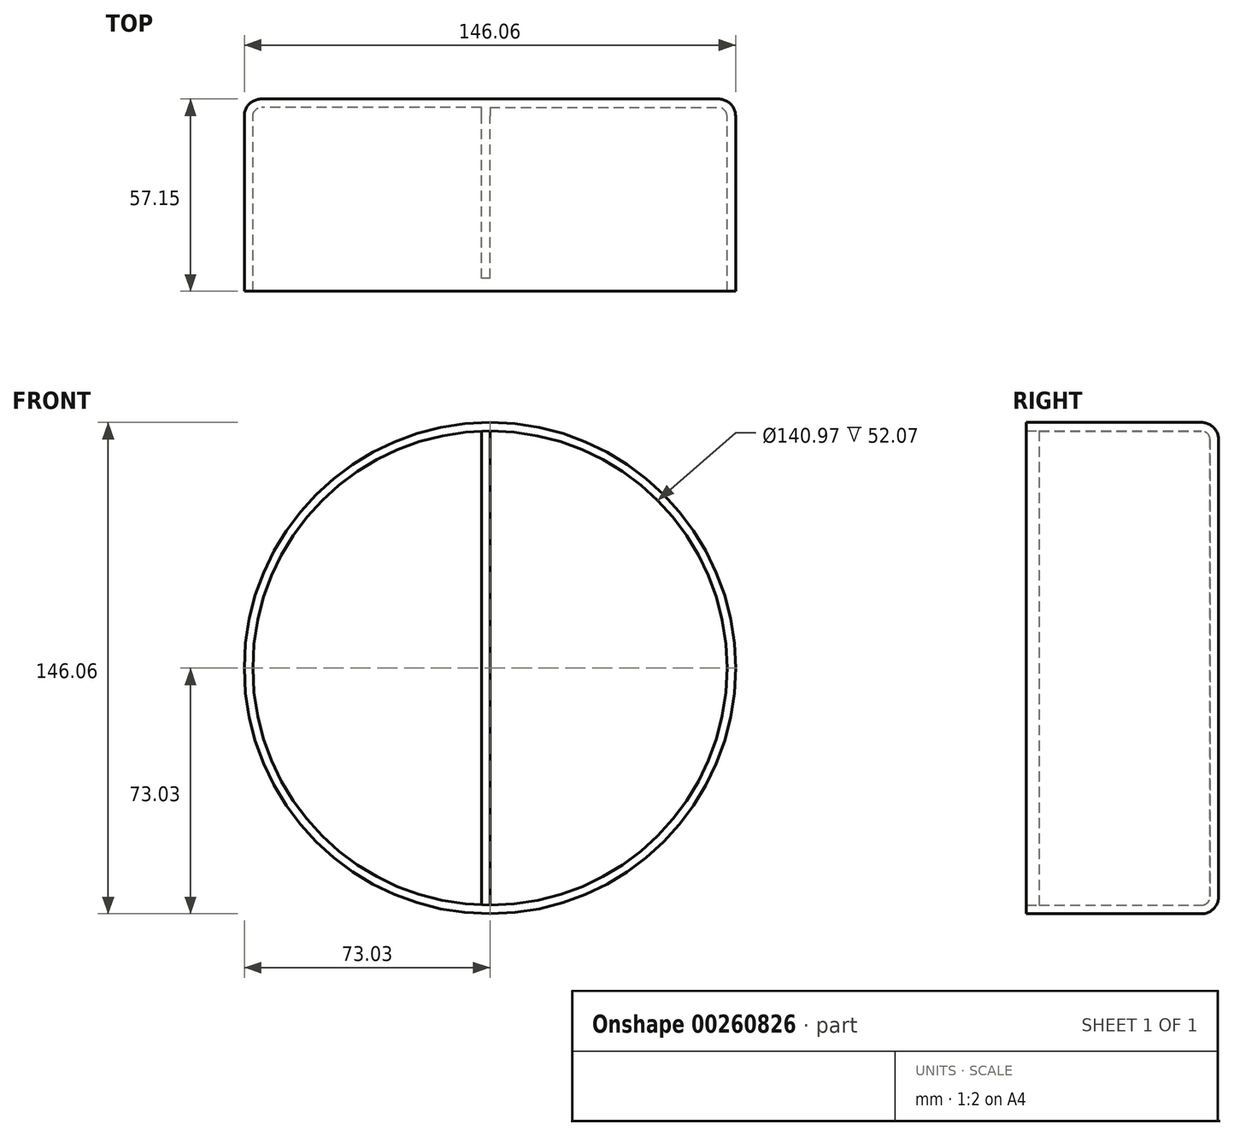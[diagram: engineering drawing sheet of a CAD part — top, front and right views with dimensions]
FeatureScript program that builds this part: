
annotation { "Feature Type Name" : "Feature", "Feature Type Description" : "" }
export const myFeature = defineFeature(function(context is Context, id is Id, definition is map)
    precondition{}
    {
        {
            var Q0;
            Q0=qCreatedBy(makeId("Front.planeOp"),FACE);
            var sketch = newSketch(context, id + "F0", { "sketchPlane" : qUnion([Q0])});
            skCircle(sketch, "E0", {"center": v(0, 0) * mm, "radius": 73.03 * mm});
            skSolve(sketch);
        }
        {
            var Q0;
            Q0=makeQuery(id+"F0.imprint","IMPRINT",FACE,{"disambiguationData":[TD([[makeQuery(id+"F0.imprint","IMPRINT",EDGE,{"derivedFrom":sQuery(id+"F0.wireOp",EDGE,"E0")}),1.0]])]});
            extrude(context, id + "F1", {"entities" : qUnion([Q0]), "depth" : 57.15 * mm});
        }
        {
            var Q0;
            Q0=makeQuery(id+"F1.opExtrude","CAP_FACE",FACE,{"disambiguationData":[OSD([sQuery(id+"F0.wireOp",EDGE,"E0")])],"isStart":false});
            shell(context, id + "F2", {"entities" : qUnion([Q0]), "thickness" : 2.54 * mm});
        }
        {
            var Q0;
            Q0=makeQuery(id+"F1.opExtrude","CAP_EDGE",EDGE,{"disambiguationData":[OSD([sQuery(id+"F0.wireOp",EDGE,"E0")])],"isStart":true});
            fillet(context, id + "F3", {"entities" : qUnion([Q0]), "radius" : 5.08 * mm, "tangentPropagation" : true, "allowEdgeOverflow" : false});
        }
        {
            var Q0;
            {var subQ0=sQuery(id+"F0.wireOp",EDGE,"E0");Q0=makeQuery(id+"F2.opShell","OFFSET_FACE",FACE,{"disambiguationData":[OSD([subQ0]),TDD([makeQuery(id+"F1.opExtrude","CAP_FACE",FACE,{"disambiguationData":[OSD([subQ0])],"isStart":true})])]});}
            var sketch = newSketch(context, id + "F4", { "sketchPlane" : qUnion([Q0])});
            skLineSegment(sketch, "E1", {"start": v(0, 70.48) * mm, "end": v(0, -70.48) * mm});
            skSolve(sketch);
        }
        {
            var Q0;
            {var subQ0=sQuery(id+"F4.wireOp",EDGE,"E1");Q0=makeQuery(id+"F4.imprint","IMPRINT",FACE,{"disambiguationData":[TD([[makeQuery(id+"F4.imprint","IMPRINT",EDGE,{"derivedFrom":subQ0}),-1.0]])]});}
            extrude(context, id + "F5", {"entities" : qUnion([Q0]), "operationType" : NewBodyOperationType.ADD, "depth" : 50.8 * mm});
        }
        {
            var Q0;
            Q0=makeQuery(id+"F5.opExtrude","CAP_FACE",FACE,{"disambiguationData":[OSD([sQuery(id+"F0.wireOp",EDGE,"E0"),sQuery(id+"F4.wireOp",EDGE,"E1")])],"isStart":false});
            shell(context, id + "F6", {"entities" : qUnion([Q0]), "thickness" : 2.54 * mm});
        }
        {
            var Q0;
            {var subQ0=sQuery(id+"F0.wireOp",EDGE,"E0");Q0=makeQuery(id+"F2.opShell","OFFSET_FACE",FACE,{"disambiguationData":[OSD([subQ0]),TDD([makeQuery(id+"F1.opExtrude","CAP_FACE",FACE,{"disambiguationData":[OSD([subQ0])],"isStart":true})])]});}
            extrude(context, id + "F7", {"entities" : qUnion([Q0]), "operationType" : NewBodyOperationType.ADD, "depth" : 50.8 * mm});
        }
        {
            var Q0;
            {var subQ0=sQuery(id+"F0.wireOp",EDGE,"E0");Q0=makeQuery(id+"F7.boolean.opBoolean","MERGE",FACE,{"derivedFrom":[makeQuery(id+"F5.opExtrude","CAP_FACE",FACE,{"disambiguationData":[OSD([subQ0,sQuery(id+"F4.wireOp",EDGE,"E1")])],"isStart":false}),makeQuery(id+"F7.opExtrude","CAP_FACE",FACE,{"disambiguationData":[OSD([subQ0])],"isStart":false})]});}
            shell(context, id + "F8", {"entities" : qUnion([Q0]), "thickness" : 2.54 * mm});
        }
    });
